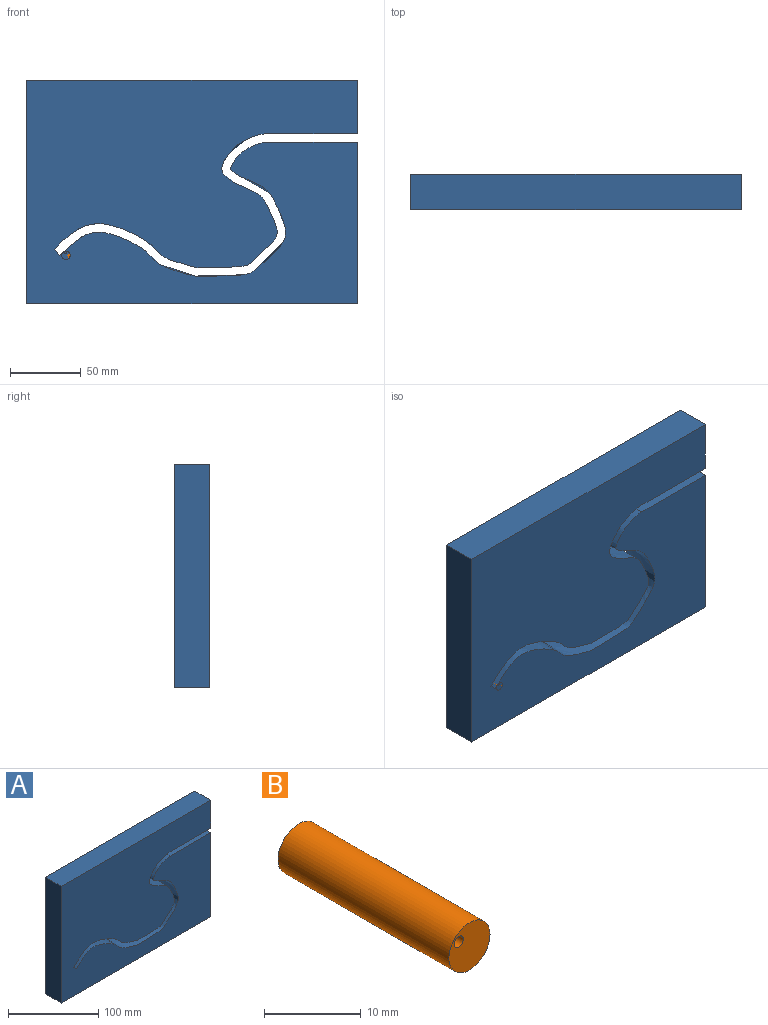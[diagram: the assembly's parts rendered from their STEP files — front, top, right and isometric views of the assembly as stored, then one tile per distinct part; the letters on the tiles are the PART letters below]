
ASSEMBLY  parts=2 mates=1
PART A: 12 faces, bbox 233.8x25x158 mm
  f0: plane 114.07x25mm, normal (1,0,0), area 2851.7mm2, adj f1,f9,f10,f11
  f1: plane 63.45x25mm, normal (0,0,1), area 1586.3mm2, adj f0,f2,f10,f11
  f2: extruded ~159.56x94.6mm, area 7130.9mm2, adj f1,f3,f10,f11
  f3: plane 25x4.34mm, normal (0.72,0,0.69), area 150mm2, adj f2,f4,f10,f11
  f4: extruded ~157.7x94.61mm, area 7286.6mm2, adj f3,f5,f10,f11
  f5: plane 63.45x25mm, normal (0,0,-1), area 1586.3mm2, adj f4,f6,f10,f11
  f6: plane 37.94x25mm, normal (1,0,0), area 948.4mm2, adj f5,f7,f10,f11
  f7: plane 233.78x25mm, normal (0,0,1), area 5844.6mm2, adj f6,f8,f10,f11
  f8: plane 158x25mm, normal (-1,0,0), area 3950.1mm2, adj f7,f9,f10,f11
  f9: plane 233.78x25mm, normal (0,0,-1), area 5844.6mm2, adj f0,f8,f10,f11
  f10: plane 233.78x158mm, normal (0,-1,0), area 34831.3mm2, adj f0,f1,f2,f3,f4,f5,f6,f7
  f11: plane 233.78x158mm, normal (0,1,0), area 34831.3mm2, adj f0,f1,f2,f3,f4,f5,f6,f7
PART B: 4 faces, bbox 6x25x6 mm
  f0: cylinder r=0.67mm len=25mm, axis (0,1,0), area 104.5mm2, adj f2,f3
  f1: cylinder r=3mm len=25mm, axis (0,1,0), area 471.2mm2, adj f2,f3
  f2: plane 6x6mm, normal (0,-1,0), area 26.9mm2, adj f0,f1
  f3: plane 6x6mm, normal (0,1,0), area 26.9mm2, adj f0,f1
PLACE A t=(-123.63,12.5,-76.14)mm fixed
PLACE B rot(axis=(-0.49,0,0.87),180deg) t=(-67.46,-12.5,29.92)mm
MATE planar A.f10 <-> B.f1  axis (0,-1,0) through (-27.4,-12.5,-35.06)mm
